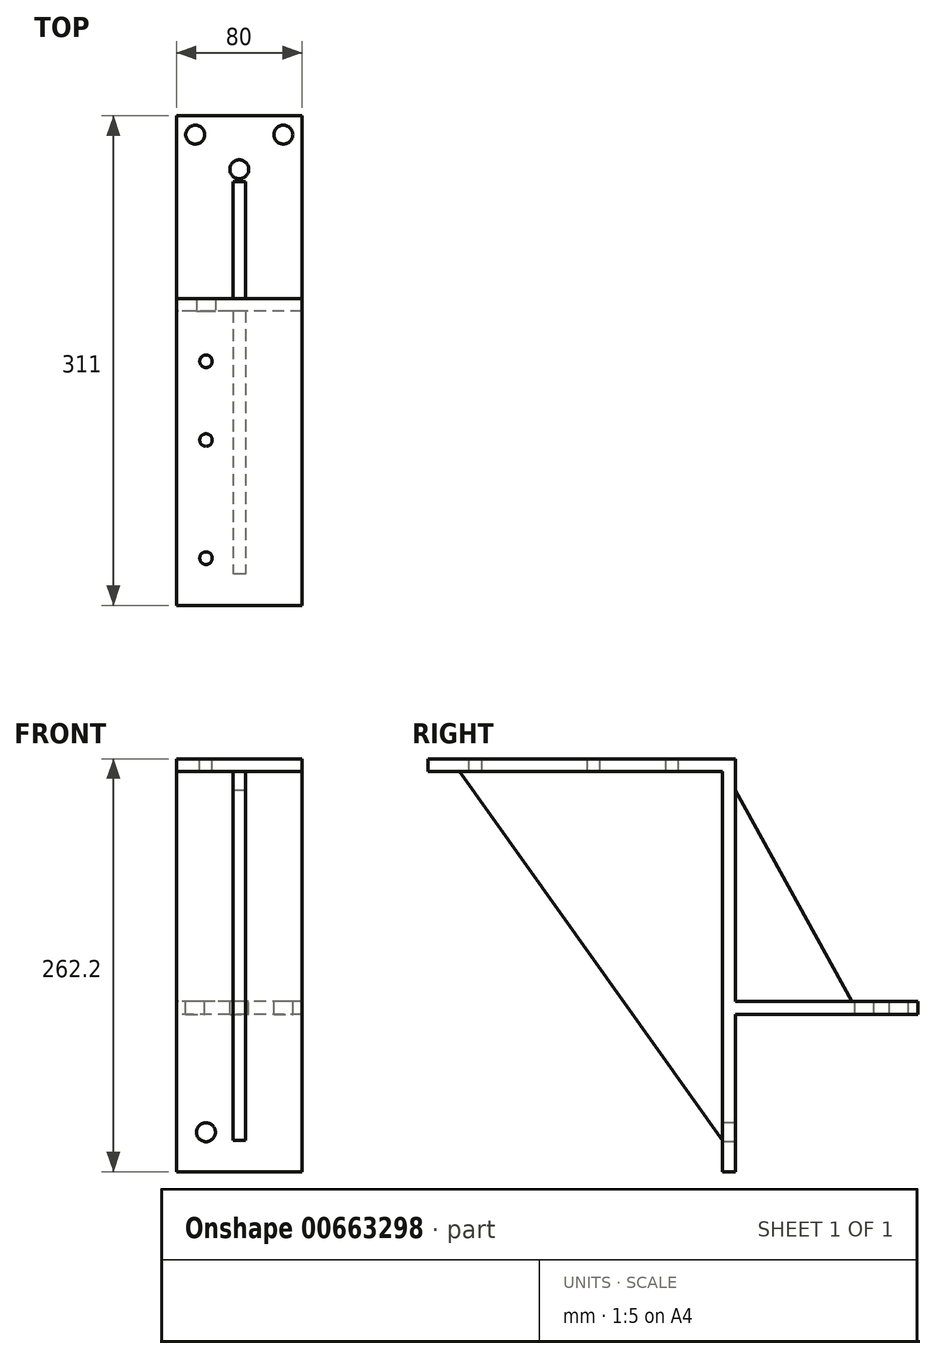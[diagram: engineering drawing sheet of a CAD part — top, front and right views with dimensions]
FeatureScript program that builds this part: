
annotation { "Feature Type Name" : "Feature", "Feature Type Description" : "" }
export const myFeature = defineFeature(function(context is Context, id is Id, definition is map)
    precondition{}
    {
        {
            var Q0;
            Q0=qCreatedBy(makeId("Right.planeOp"),FACE);
            var sketch = newSketch(context, id + "F0", { "sketchPlane" : qUnion([Q0])});
            skLineSegment(sketch, "E0", {"start": v(-195, 262.2) * mm, "end": v(0, 262.2) * mm});
            skLineSegment(sketch, "E1", {"start": v(0, 262.2) * mm, "end": v(0, 0) * mm});
            skLineSegment(sketch, "E2", {"start": v(0, 0) * mm, "end": v(-8, 0) * mm});
            skLineSegment(sketch, "E3", {"start": v(-8, 0) * mm, "end": v(-8, 254.2) * mm});
            skLineSegment(sketch, "E4", {"start": v(-8, 254.2) * mm, "end": v(-195, 254.2) * mm});
            skLineSegment(sketch, "E5", {"start": v(-195, 254.2) * mm, "end": v(-195, 262.2) * mm});
            skLineSegment(sketch, "E6", {"start": v(-175, 254.2) * mm, "end": v(-8, 20) * mm});
            skLineSegment(sketch, "E7", {"start": v(0, 108) * mm, "end": v(116, 108) * mm});
            skLineSegment(sketch, "E8", {"start": v(116, 108) * mm, "end": v(116, 100) * mm});
            skLineSegment(sketch, "E9", {"start": v(116, 100) * mm, "end": v(0, 100) * mm});
            skLineSegment(sketch, "E10", {"start": v(0, 242.2) * mm, "end": v(74.1, 108) * mm});
            skSolve(sketch);
        }
        {
            var Q0;
            {var subQ10=sQuery(id+"F0.wireOp",EDGE,"E0");Q0=makeQuery(id+"F0.imprint","IMPRINT",FACE,{"disambiguationData":[TD([[makeQuery(id+"F0.imprint","IMPRINT",EDGE,{"derivedFrom":subQ10}),-1.0]])]});}
            var Q1;
            {var subQ0=sQuery(id+"F0.wireOp",EDGE,"E8");Q1=makeQuery(id+"F0.imprint","IMPRINT",FACE,{"disambiguationData":[TD([[makeQuery(id+"F0.imprint","IMPRINT",EDGE,{"derivedFrom":subQ0}),-1.0]])]});}
            extrude(context, id + "F1", {"entities" : qUnion([Q0, Q1]), "endBound" : BoundingType.SYMMETRIC, "depth" : 80 * mm, "offsetDistance" : 25 * mm});
        }
        {
            var Q0;
            {var subQ3=sQuery(id+"F0.wireOp",EDGE,"E6");Q0=makeQuery(id+"F0.imprint","IMPRINT",FACE,{"disambiguationData":[TD([[makeQuery(id+"F0.imprint","IMPRINT",EDGE,{"derivedFrom":subQ3}),1.0]])]});}
            var Q1;
            {var subQ3=sQuery(id+"F0.wireOp",EDGE,"E10");Q1=makeQuery(id+"F0.imprint","IMPRINT",FACE,{"disambiguationData":[TD([[makeQuery(id+"F0.imprint","IMPRINT",EDGE,{"derivedFrom":subQ3}),-1.0]])]});}
            extrude(context, id + "F2", {"entities" : qUnion([Q0, Q1]), "operationType" : NewBodyOperationType.ADD, "endBound" : BoundingType.SYMMETRIC, "depth" : 8 * mm, "offsetDistance" : 25 * mm});
        }
        {
            var Q0;
            Q0=makeQuery(id+"F1.opExtrude","SWEPT_FACE",FACE,{"disambiguationData":[OSD([sQuery(id+"F0.wireOp",EDGE,"E0")])]});
            var sketch = newSketch(context, id + "F3", { "sketchPlane" : qUnion([Q0])});
            skCircle(sketch, "E11", {"center": v(-21.15, -165) * mm, "radius": 4 * mm});
            skCircle(sketch, "E12", {"center": v(-21.15, -90) * mm, "radius": 4 * mm});
            skCircle(sketch, "E13", {"center": v(-21.15, -40) * mm, "radius": 4 * mm});
            skSolve(sketch);
        }
        {
            var Q0;
            Q0=makeQuery(id+"F3.imprint","IMPRINT",FACE,{"disambiguationData":[TD([[makeQuery(id+"F3.imprint","IMPRINT",EDGE,{"derivedFrom":sQuery(id+"F3.wireOp",EDGE,"E13")}),1.0]])]});
            var Q1;
            Q1=makeQuery(id+"F3.imprint","IMPRINT",FACE,{"disambiguationData":[TD([[makeQuery(id+"F3.imprint","IMPRINT",EDGE,{"derivedFrom":sQuery(id+"F3.wireOp",EDGE,"E12")}),1.0]])]});
            var Q2;
            Q2=makeQuery(id+"F3.imprint","IMPRINT",FACE,{"disambiguationData":[TD([[makeQuery(id+"F3.imprint","IMPRINT",EDGE,{"derivedFrom":sQuery(id+"F3.wireOp",EDGE,"E11")}),1.0]])]});
            extrude(context, id + "F4", {"entities" : qUnion([Q0, Q1, Q2]), "operationType" : NewBodyOperationType.REMOVE, "endBound" : BoundingType.THROUGH_ALL, "oppositeDirection" : true, "depth" : 25 * mm, "offsetDistance" : 25 * mm});
        }
        {
            var Q0;
            Q0=makeQuery(id+"F1.opExtrude","SWEPT_FACE",FACE,{"disambiguationData":[OSD([sQuery(id+"F0.wireOp",EDGE,"E3")])]});
            var sketch = newSketch(context, id + "F5", { "sketchPlane" : qUnion([Q0])});
            skCircle(sketch, "E14", {"center": v(-21.15, 25) * mm, "radius": 6 * mm});
            skSolve(sketch);
        }
        {
            var Q0;
            Q0=makeQuery(id+"F5.imprint","IMPRINT",FACE,{"disambiguationData":[TD([[makeQuery(id+"F5.imprint","IMPRINT",EDGE,{"derivedFrom":sQuery(id+"F5.wireOp",EDGE,"E14")}),1.0]])]});
            extrude(context, id + "F6", {"entities" : qUnion([Q0]), "operationType" : NewBodyOperationType.REMOVE, "endBound" : BoundingType.THROUGH_ALL, "oppositeDirection" : true, "depth" : 25 * mm, "offsetDistance" : 25 * mm});
        }
        {
            var Q0;
            Q0=makeQuery(id+"F1.opExtrude","SWEPT_FACE",FACE,{"disambiguationData":[OSD([sQuery(id+"F0.wireOp",EDGE,"E7")])]});
            var sketch = newSketch(context, id + "F7", { "sketchPlane" : qUnion([Q0])});
            skCircle(sketch, "E15", {"center": v(28, 104) * mm, "radius": 6 * mm});
            skCircle(sketch, "E16", {"center": v(-28, 104) * mm, "radius": 6 * mm});
            skCircle(sketch, "E17", {"center": v(0, 82) * mm, "radius": 6 * mm});
            skSolve(sketch);
        }
        {
            var Q0;
            Q0=makeQuery(id+"F7.imprint","IMPRINT",FACE,{"disambiguationData":[TD([[makeQuery(id+"F7.imprint","IMPRINT",EDGE,{"derivedFrom":sQuery(id+"F7.wireOp",EDGE,"E16")}),1.0]])]});
            var Q1;
            Q1=makeQuery(id+"F7.imprint","IMPRINT",FACE,{"disambiguationData":[TD([[makeQuery(id+"F7.imprint","IMPRINT",EDGE,{"derivedFrom":sQuery(id+"F7.wireOp",EDGE,"E17")}),1.0]])]});
            var Q2;
            Q2=makeQuery(id+"F7.imprint","IMPRINT",FACE,{"disambiguationData":[TD([[makeQuery(id+"F7.imprint","IMPRINT",EDGE,{"derivedFrom":sQuery(id+"F7.wireOp",EDGE,"E15")}),1.0]])]});
            extrude(context, id + "F8", {"entities" : qUnion([Q0, Q1, Q2]), "operationType" : NewBodyOperationType.REMOVE, "endBound" : BoundingType.THROUGH_ALL, "oppositeDirection" : true, "depth" : 25 * mm, "offsetDistance" : 25 * mm});
        }
    });
